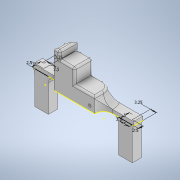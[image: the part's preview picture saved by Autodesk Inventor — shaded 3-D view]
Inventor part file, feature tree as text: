
AUTODESK INVENTOR PART (.ipt)
format: ipt  version: 2022 (Build 260153000, 153)  size: 275,968 bytes
history: native  units: mm
features: fillet x5, extrude x4, sketch x4, other x2, hole x1
ambient origin geometry x8: Origin, YZ Plane, XZ Plane, XY Plane, X Axis, Y Axis, Z Axis, Center Point
bodies: Solido1 (feature_tree)
feature tree (16):
  extrude  "Estrusione1"  Depth=22.0mm
  extrude  "Estrusione2"  Depth=20.0mm
  fillet  "Raccordo1"  Radius=10.0mm
  fillet  "Raccordo2"  Radius=16.5mm
  sketch  "Schizzo3"
  extrude  "Estrusione3"  Depth=5.0mm
  hole  "Foro1"  [1 undecoded]
  extrude  "Estrusione4"  Depth=5.0mm
  fillet  "Raccordo4"  Radius=16.5mm
  fillet  "Raccordo5"  [1 undecoded]
  fillet  "Raccordo6"  Radius=2.0mm
  sketch  "Schizzo1"
  sketch  "Schizzo2"
  other  "Linea chiusa proiettata1"
  sketch  "Schizzo4"
  other  "Linea chiusa proiettata2"
note: 2 required parameter values undecoded (feature->parameter linkage not recoverable at this tier; creation-order binding heuristic only, values carry confidence <= 0.55)
